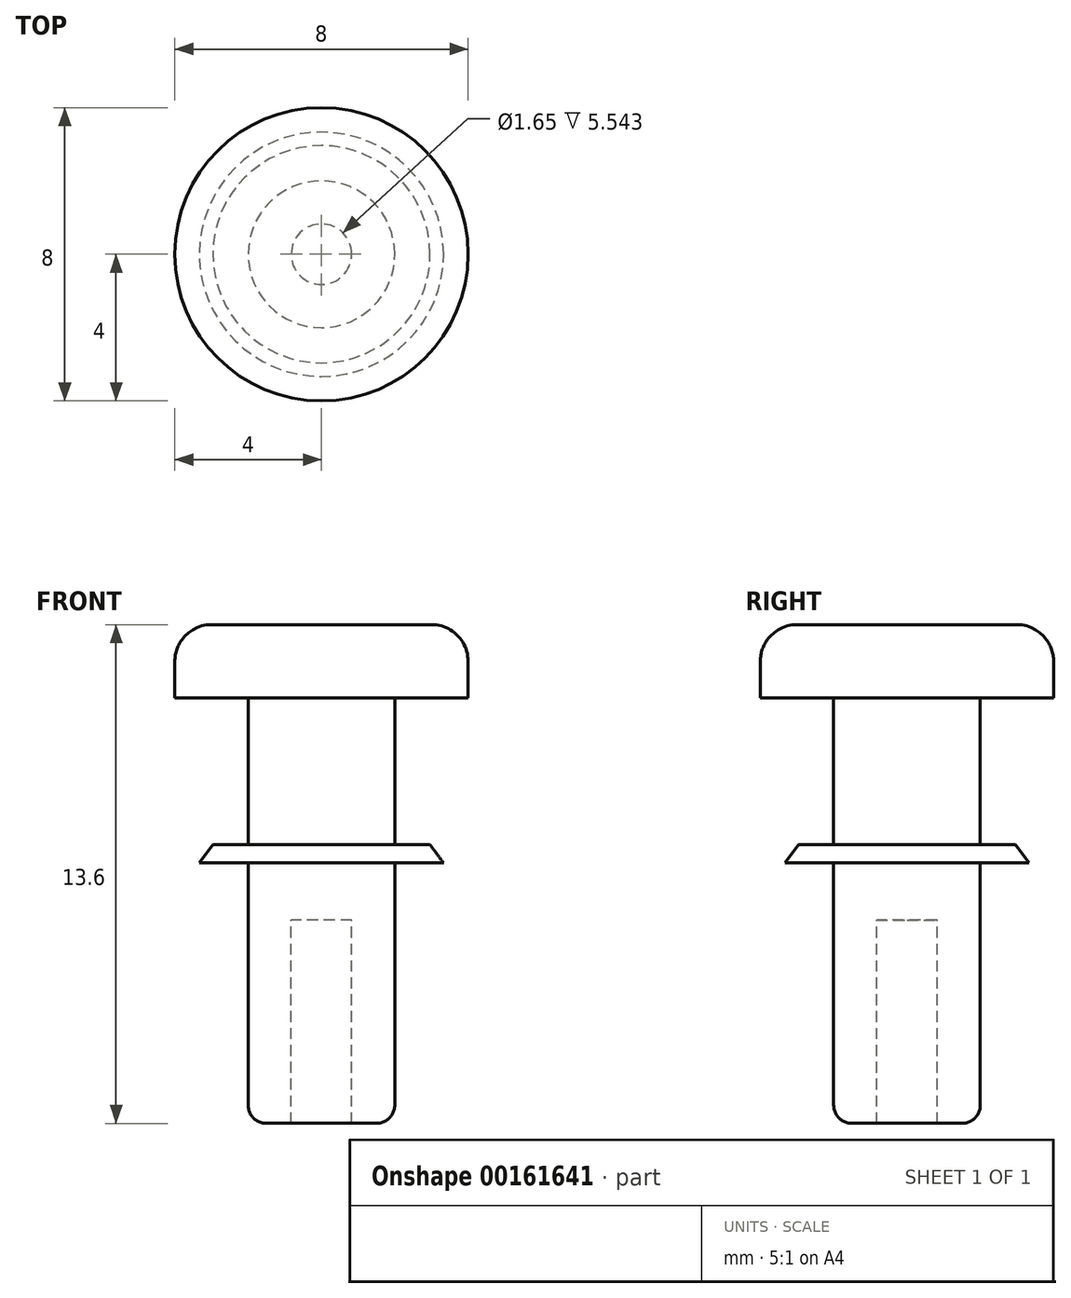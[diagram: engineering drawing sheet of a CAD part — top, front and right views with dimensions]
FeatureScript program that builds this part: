
annotation { "Feature Type Name" : "Feature", "Feature Type Description" : "" }
export const myFeature = defineFeature(function(context is Context, id is Id, definition is map)
    precondition{}
    {
        {
            var Q0;
            Q0=qCreatedBy(makeId("Right.planeOp"),FACE);
            var sketch = newSketch(context, id + "F0", { "sketchPlane" : qUnion([Q0])});
            skLineSegment(sketch, "E0", {"start": v(0, 13.95) * mm, "end": v(-3, 13.95) * mm});
            skLineSegment(sketch, "E1", {"start": v(-4, 12.95) * mm, "end": v(-4, 11.95) * mm});
            skLineSegment(sketch, "E2", {"start": v(-4, 11.95) * mm, "end": v(-2, 11.95) * mm});
            skLineSegment(sketch, "E3", {"start": v(-2, 11.95) * mm, "end": v(-2, 7.95) * mm});
            skLineSegment(sketch, "E4", {"start": v(-2, 7.95) * mm, "end": v(-2.96, 7.95) * mm});
            skLineSegment(sketch, "E5", {"start": v(-2.96, 7.95) * mm, "end": v(-3.33, 7.45) * mm});
            skLineSegment(sketch, "E6", {"start": v(-3.33, 7.45) * mm, "end": v(-2, 7.45) * mm});
            skLineSegment(sketch, "E7", {"start": v(-2, 7.45) * mm, "end": v(-2, 0.85) * mm});
            skLineSegment(sketch, "E8", {"start": v(-1.5, 0.35) * mm, "end": v(-0.83, 0.35) * mm});
            skPoint(sketch, "E9.visualSharp", {"position": v(-4, 13.95) * mm});
            skArc(sketch, "E9.filletArc", {"start": v(-3, 13.95) * mm, "mid": v(-3.7, 13.66) * mm, "end": v(-4, 12.95) * mm});
            skPoint(sketch, "E10.orphan", {"position": v(0, 11.95) * mm});
            skPoint(sketch, "E11.orphan", {"position": v(0, 7.45) * mm});
            skLineSegment(sketch, "E12", {"start": v(0, 13.95) * mm, "end": v(0, 5.9) * mm});
            skLineSegment(sketch, "E13", {"start": v(-0.83, 0.35) * mm, "end": v(-0.83, 5.9) * mm});
            skLineSegment(sketch, "E14", {"start": v(-0.83, 5.9) * mm, "end": v(0, 5.9) * mm});
            skPoint(sketch, "E15.orphan", {"position": v(0, 0.35) * mm});
            skPoint(sketch, "E16.visualSharp", {"position": v(-2, 0.35) * mm});
            skArc(sketch, "E16.filletArc", {"start": v(-2, 0.85) * mm, "mid": v(-1.85, 0.5) * mm, "end": v(-1.5, 0.35) * mm});
            skSolve(sketch);
        }
        {
            var Q0;
            Q0 = qSketchRegion(id + "F0", true);
            var Q1;
            Q1=sQuery(id+"F0.wireOp",EDGE,"E12");
            revolve(context, id + "F1", {"entities" : qUnion([Q0]), "axis" : qUnion([Q1]), "revolveType" : RevolveType.FULL});
        }
    });
